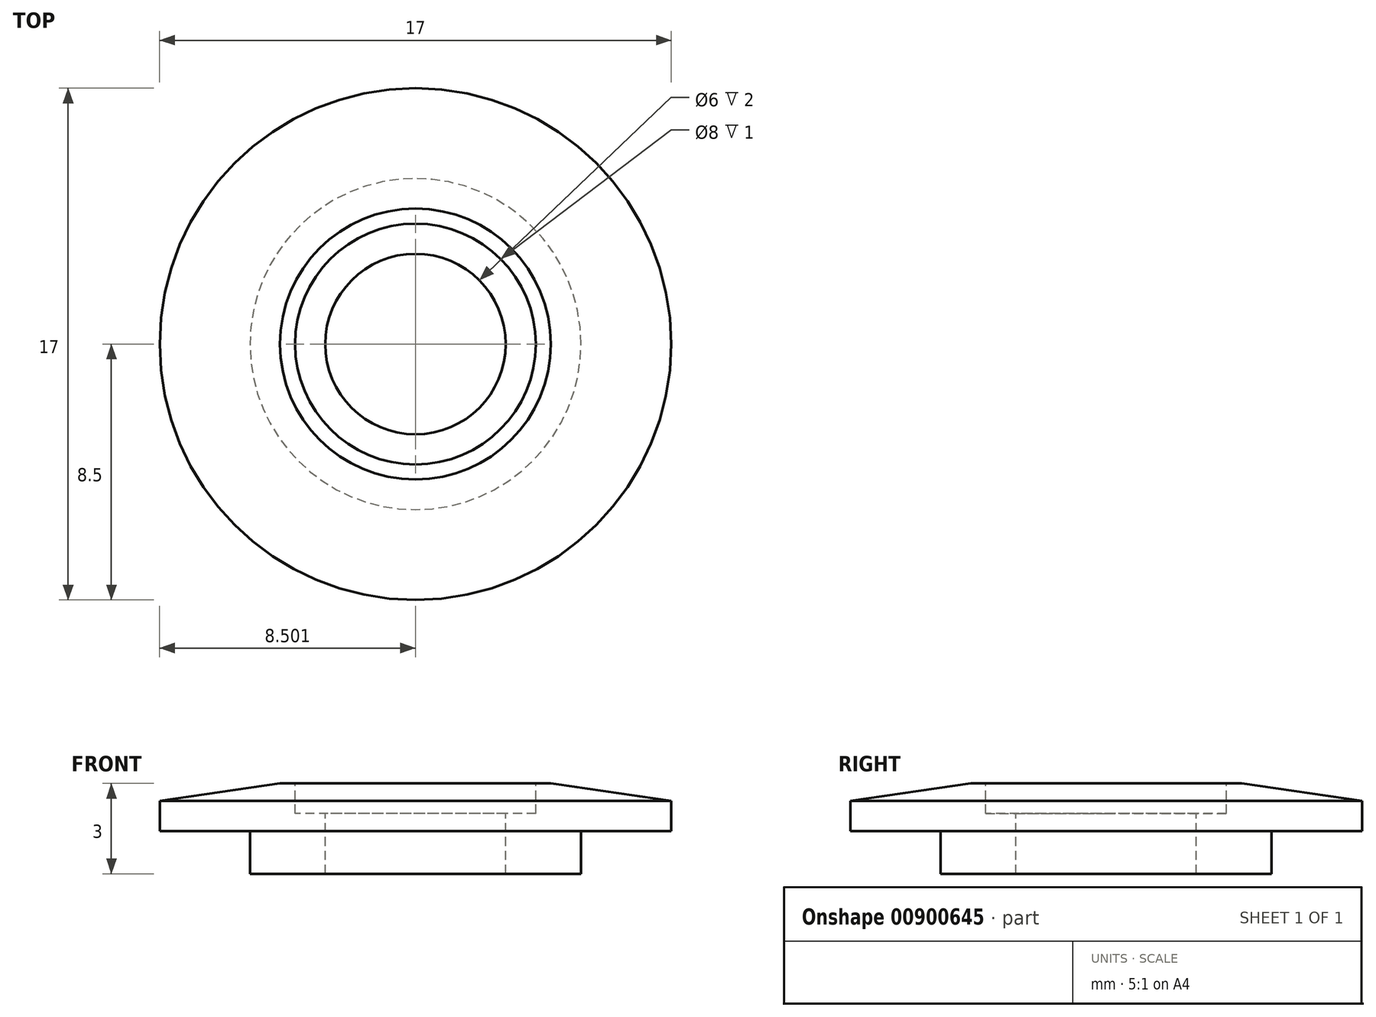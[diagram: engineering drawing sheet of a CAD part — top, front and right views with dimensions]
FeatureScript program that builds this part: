
annotation { "Feature Type Name" : "Feature", "Feature Type Description" : "" }
export const myFeature = defineFeature(function(context is Context, id is Id, definition is map)
    precondition{}
    {
        {
            var Q0;
            Q0=qCreatedBy(makeId("Front.planeOp"),FACE);
            var sketch = newSketch(context, id + "F0", { "sketchPlane" : qUnion([Q0])});
            skLineSegment(sketch, "E0", {"start": v(6.94, 2.2) * mm, "end": v(9.44, 2.2) * mm});
            skLineSegment(sketch, "E1", {"start": v(9.44, 2.2) * mm, "end": v(9.44, 3.62) * mm});
            skLineSegment(sketch, "E2", {"start": v(9.44, 3.62) * mm, "end": v(12.44, 3.62) * mm});
            skLineSegment(sketch, "E3", {"start": v(12.44, 3.62) * mm, "end": v(12.44, 4.62) * mm});
            skLineSegment(sketch, "E4", {"start": v(12.44, 4.62) * mm, "end": v(8.44, 5.2) * mm});
            skLineSegment(sketch, "E5", {"start": v(6.94, 2.2) * mm, "end": v(6.94, 4.2) * mm});
            skLineSegment(sketch, "E6", {"start": v(6.94, 4.2) * mm, "end": v(7.94, 4.2) * mm});
            skLineSegment(sketch, "E7", {"start": v(7.94, 4.2) * mm, "end": v(7.94, 5.2) * mm});
            skLineSegment(sketch, "E8", {"start": v(7.94, 5.2) * mm, "end": v(8.44, 5.2) * mm});
            skLineSegment(sketch, "E9", {"start": v(3.94, 8.24) * mm, "end": v(3.94, 6.75) * mm, "construction": true});
            skSolve(sketch);
        }
        {
            var Q0;
            Q0=makeQuery(id+"F0.imprint","IMPRINT",FACE,{"disambiguationData":[TD([[makeQuery(id+"F0.imprint","IMPRINT",EDGE,{"derivedFrom":sQuery(id+"F0.wireOp",EDGE,"E0")}),1.0]])]});
            var Q1;
            Q1=sQuery(id+"F0.wireOp",EDGE,"E9");
            revolve(context, id + "F1", {"surfaceOperationType" : NewSurfaceOperationType.NEW, "entities" : qUnion([Q0]), "axis" : qUnion([Q1]), "revolveType" : RevolveType.FULL});
        }
    });
